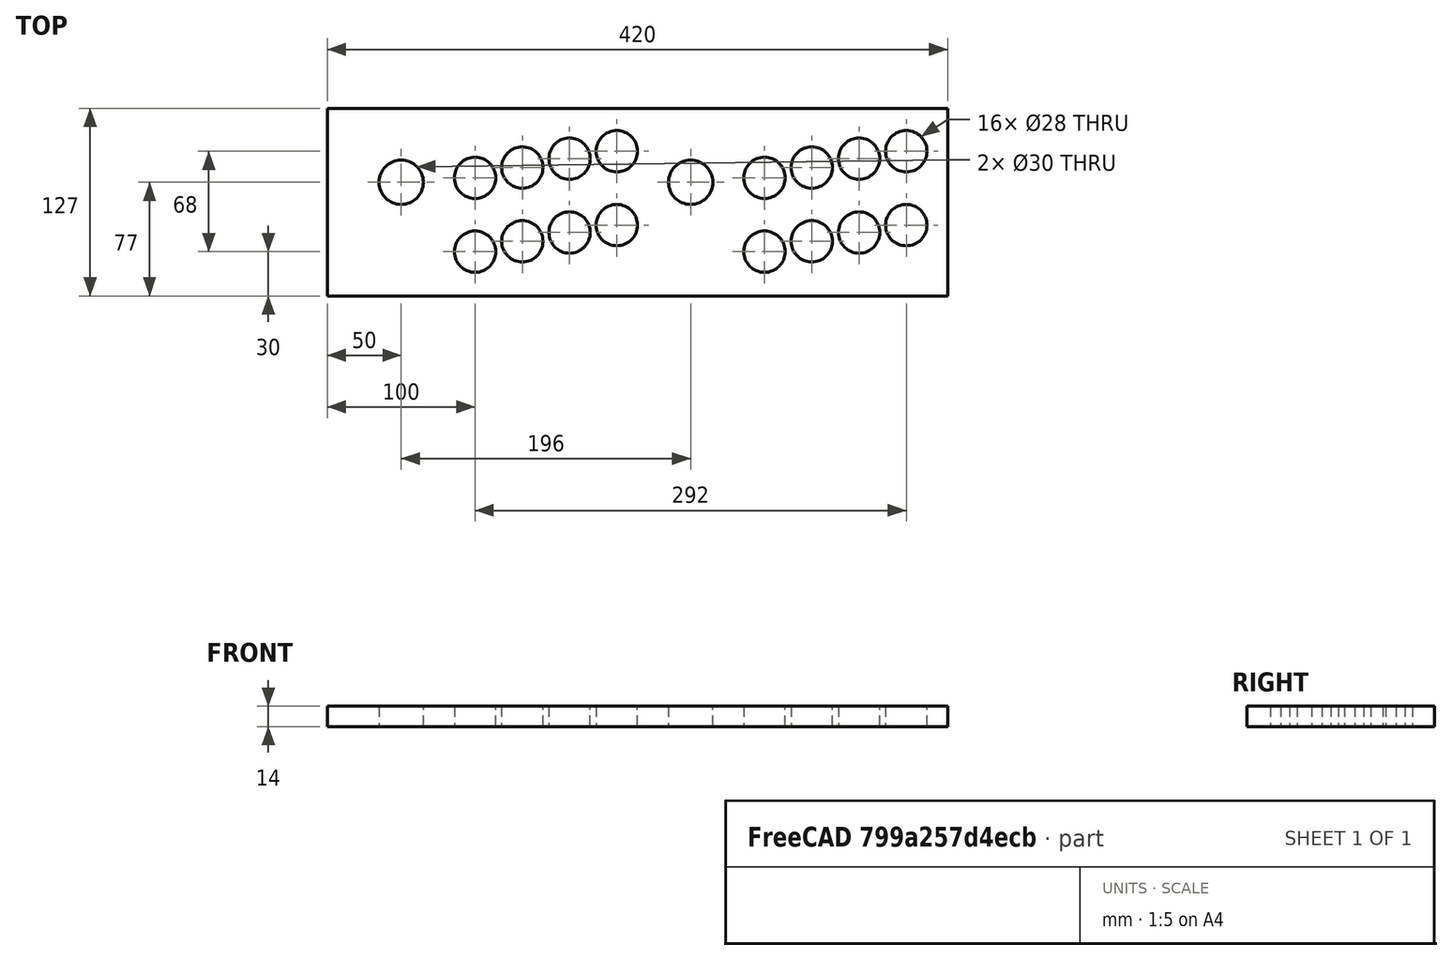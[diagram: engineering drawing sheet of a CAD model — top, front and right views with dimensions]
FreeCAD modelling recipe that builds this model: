
FCSTD DOCUMENT  (FreeCAD 0.18R16131 (Git))
Label: Joystick_plate
License: All rights reserved
LicenseURL: http://en.wikipedia.org/wiki/All_rights_reserved
objects: Sketcher::SketchObject×1, PartDesign::Pad×1, PartDesign::Body×1
note: 4 computed .brp shape members not serialized (recipe doc carries the construction recipe); baked Part::Feature solids carry a one-line shape summary decoded from their .brp

FEATURE [Sketcher::SketchObject] Sketch
  MapMode = 5
  Support = -> [XY_Plane]
  sketch-geometry (46):
    g0: LineSegment StartX=0 StartY=0 StartZ=0 EndX=420 EndY=0 EndZ=0
    g1: LineSegment StartX=420 StartY=0 StartZ=0 EndX=420 EndY=127 EndZ=0
    g2: LineSegment StartX=420 StartY=127 StartZ=0 EndX=0 EndY=127 EndZ=0
    g3: LineSegment StartX=0 StartY=127 StartZ=0 EndX=0 EndY=0 EndZ=0
    g4: Circle CenterX=50 CenterY=77 CenterZ=0 NormalX=0 NormalY=0 NormalZ=1 AngleXU=0 Radius=15
    g5: Circle CenterX=100 CenterY=80 CenterZ=0 NormalX=0 NormalY=0 NormalZ=1 AngleXU=0 Radius=14
    g6: Circle CenterX=132 CenterY=87 CenterZ=0 NormalX=0 NormalY=0 NormalZ=1 AngleXU=0 Radius=14
    g7: Circle CenterX=164 CenterY=93 CenterZ=0 NormalX=0 NormalY=0 NormalZ=1 AngleXU=0 Radius=14
    g8: Circle CenterX=196 CenterY=98 CenterZ=0 NormalX=0 NormalY=0 NormalZ=1 AngleXU=0 Radius=14
    g9: LineSegment [constr] StartX=100 StartY=80 StartZ=0 EndX=100 EndY=87 EndZ=0
    g10: LineSegment [constr] StartX=132 StartY=87 StartZ=0 EndX=100 EndY=87 EndZ=0
    g11: LineSegment [constr] StartX=132 StartY=87 StartZ=0 EndX=132 EndY=93 EndZ=0
    g12: LineSegment [constr] StartX=132 StartY=93 StartZ=0 EndX=164 EndY=93 EndZ=0
    g13: LineSegment [constr] StartX=164 StartY=93 StartZ=0 EndX=164 EndY=98 EndZ=0
    g14: LineSegment [constr] StartX=196 StartY=98 StartZ=0 EndX=164 EndY=98 EndZ=0
    g15: Circle CenterX=100 CenterY=30 CenterZ=0 NormalX=0 NormalY=0 NormalZ=1 AngleXU=0 Radius=14
    g16: Circle CenterX=132 CenterY=37 CenterZ=0 NormalX=0 NormalY=0 NormalZ=1 AngleXU=0 Radius=14
    g17: Circle CenterX=164 CenterY=43 CenterZ=0 NormalX=0 NormalY=0 NormalZ=1 AngleXU=0 Radius=14
    g18: Circle CenterX=196 CenterY=48 CenterZ=0 NormalX=0 NormalY=0 NormalZ=1 AngleXU=0 Radius=14
    g19: LineSegment [constr] StartX=100 StartY=30 StartZ=0 EndX=100 EndY=37 EndZ=0
    g20: LineSegment [constr] StartX=100 StartY=37 StartZ=0 EndX=132 EndY=37 EndZ=0
    g21: LineSegment [constr] StartX=132 StartY=37 StartZ=0 EndX=132 EndY=43 EndZ=0
    g22: LineSegment [constr] StartX=132 StartY=43 StartZ=0 EndX=164 EndY=43 EndZ=0
    g23: LineSegment [constr] StartX=164 StartY=43 StartZ=0 EndX=164 EndY=48 EndZ=0
    g24: LineSegment [constr] StartX=164 StartY=48 StartZ=0 EndX=196 EndY=48 EndZ=0
    g25: Circle CenterX=246 CenterY=77 CenterZ=0 NormalX=0 NormalY=0 NormalZ=1 AngleXU=0 Radius=15
    g26: LineSegment [constr] StartX=296 StartY=80 StartZ=0 EndX=296 EndY=87 EndZ=0
    g27: LineSegment [constr] StartX=296 StartY=87 StartZ=0 EndX=328 EndY=87 EndZ=0
    g28: LineSegment [constr] StartX=328 StartY=87 StartZ=0 EndX=328 EndY=93 EndZ=0
    g29: LineSegment [constr] StartX=328 StartY=93 StartZ=0 EndX=360 EndY=93 EndZ=0
    g30: LineSegment [constr] StartX=360 StartY=93 StartZ=0 EndX=360 EndY=98 EndZ=0
    g31: LineSegment [constr] StartX=360 StartY=98 StartZ=0 EndX=392 EndY=98 EndZ=0
    g32: LineSegment [constr] StartX=296 StartY=30 StartZ=0 EndX=296 EndY=37 EndZ=0
    g33: LineSegment [constr] StartX=296 StartY=37 StartZ=0 EndX=328 EndY=37 EndZ=0
    g34: LineSegment [constr] StartX=328 StartY=37 StartZ=0 EndX=328 EndY=43 EndZ=0
    g35: LineSegment [constr] StartX=328 StartY=43 StartZ=0 EndX=360 EndY=43 EndZ=0
    g36: LineSegment [constr] StartX=360 StartY=43 StartZ=0 EndX=360 EndY=48 EndZ=0
    g37: LineSegment [constr] StartX=360 StartY=48 StartZ=0 EndX=392 EndY=48 EndZ=0
    g38: Circle CenterX=296 CenterY=80 CenterZ=0 NormalX=0 NormalY=0 NormalZ=1 AngleXU=0 Radius=14
    g39: Circle CenterX=328 CenterY=87 CenterZ=0 NormalX=0 NormalY=0 NormalZ=1 AngleXU=0 Radius=14
    g40: Circle CenterX=360 CenterY=93 CenterZ=0 NormalX=0 NormalY=0 NormalZ=1 AngleXU=0 Radius=14
    g41: Circle CenterX=392 CenterY=98 CenterZ=0 NormalX=0 NormalY=0 NormalZ=1 AngleXU=0 Radius=14
    g42: Circle CenterX=392 CenterY=48 CenterZ=0 NormalX=0 NormalY=0 NormalZ=1 AngleXU=0 Radius=14
    g43: Circle CenterX=360 CenterY=43 CenterZ=0 NormalX=0 NormalY=0 NormalZ=1 AngleXU=0 Radius=14
    g44: Circle CenterX=328 CenterY=37 CenterZ=0 NormalX=0 NormalY=0 NormalZ=1 AngleXU=0 Radius=14
    g45: Circle CenterX=296 CenterY=30 CenterZ=0 NormalX=0 NormalY=0 NormalZ=1 AngleXU=0 Radius=14
  constraints (125):
    c: Coincident(g0,g1)
    c: Coincident(g1,g2)
    c: Coincident(g2,g3)
    c: Coincident(g3,g0)
    c: Horizontal(g0)
    c: Horizontal(g2)
    c: Vertical(g1)
    c: Vertical(g3)
    c: Coincident(g0,g-1)
    c: DistanceX(g2,g2) = 420
    c: DistanceY(g3,g3) = 127
    c: DistanceX(g2,g4) = 50
    c: Radius(g4) = 15
    c: Diameter(g5) = 28
    c: Coincident(g9,g5)
    c: Vertical(g9)
    c: Coincident(g10,g6)
    c: Coincident(g10,g9)
    c: Horizontal(g10)
    c: Coincident(g11,g6)
    c: Vertical(g11)
    c: Coincident(g12,g11)
    c: Coincident(g12,g7)
    c: Horizontal(g12)
    c: Coincident(g13,g7)
    c: Vertical(g13)
    c: Coincident(g14,g8)
    c: Coincident(g14,g13)
    c: Equal(g10,g12)
    c: Equal(g12,g14)
    c: Coincident(g19,g15)
    c: Vertical(g19)
    c: Coincident(g20,g19)
    c: Coincident(g20,g16)
    c: Coincident(g21,g16)
    c: Coincident(g22,g21)
    c: Coincident(g22,g17)
    c: Coincident(g23,g17)
    c: Vertical(g23)
    c: Coincident(g24,g23)
    c: Coincident(g24,g18)
    c: Horizontal(g24)
    c: Horizontal(g22)
    c: Horizontal(g20)
    c: Vertical(g21)
    c: Equal(g14,g24)
    c: Equal(g24,g22)
    c: Equal(g22,g20)
    c: Equal(g13,g23)
    c: Equal(g11,g21)
    c: Equal(g9,g19)
    c: Equal(g5,g6)
    c: Equal(g6,g7)
    c: Equal(g7,g8)
    c: Equal(g8,g18)
    c: Equal(g18,g17)
    c: Equal(g17,g15)
    c: Equal(g15,g16)
    c: Horizontal(g14)
    c: DistanceY(g15,g5) = 50
    c: DistanceY(g0,g15) = 30
    c: DistanceY(g4,g2) = 50
    c: DistanceX(g4,g5) = 50
    c: DistanceX(g10,g10) = 32
    c: Vertical(g5,g15)
    c: DistanceY(g9,g9) = 7
    c: DistanceY(g11,g11) = 6
    c: DistanceY(g13,g13) = 5
    c: Horizontal(g4,g25)
    c: Equal(g4,g25)
    c: Vertical(g26)
    c: Coincident(g27,g26)
    c: Horizontal(g27)
    c: Coincident(g28,g27)
    c: Vertical(g28)
    c: Coincident(g29,g28)
    c: Horizontal(g29)
    c: Coincident(g30,g29)
    c: Vertical(g30)
    c: Coincident(g31,g30)
    c: Horizontal(g31)
    c: Vertical(g32)
    c: Coincident(g33,g32)
    c: Horizontal(g33)
    c: Coincident(g34,g33)
    c: Vertical(g34)
    c: Coincident(g35,g34)
    c: Horizontal(g35)
    c: Coincident(g36,g35)
    c: Vertical(g36)
    c: Coincident(g37,g36)
    c: Horizontal(g37)
    c: Vertical(g32,g26)
    c: Equal(g26,g32)
    c: Equal(g32,g9)
    c: Equal(g27,g33)
    c: Equal(g33,g10)
    c: Equal(g28,g34)
    c: Equal(g34,g11)
    c: Equal(g22,g35)
    c: Equal(g35,g29)
    c: Equal(g30,g36)
    c: Equal(g36,g13)
    c: Equal(g31,g37)
    c: Equal(g37,g14)
    c: Coincident(g38,g26)
    c: Coincident(g39,g27)
    c: Coincident(g40,g29)
    c: Coincident(g41,g31)
    c: Coincident(g42,g37)
    c: Coincident(g43,g35)
    c: Coincident(g44,g33)
    c: Coincident(g45,g32)
    c: Equal(g5,g38)
    c: Equal(g38,g39)
    c: Equal(g39,g40)
    c: Equal(g40,g41)
    c: Equal(g41,g42)
    c: Equal(g42,g43)
    c: Equal(g43,g44)
    c: Equal(g44,g45)
    c: Horizontal(g45,g15)
    c: Horizontal(g38,g5)
    c: DistanceX(g25,g38) = 50
    c: DistanceX(g8,g25) = 50
FEATURE [PartDesign::Pad] Pad
  Length = 14
  Length2 = 100
  Profile = -> Sketch
  Type = 0
FEATURE [PartDesign::Body] Body
  Group = -> [Sketch,Pad]
  Origin = -> Origin
  Tip = -> Pad
